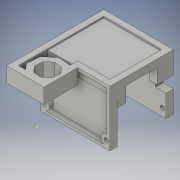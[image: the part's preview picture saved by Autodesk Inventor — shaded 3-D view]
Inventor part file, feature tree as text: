
AUTODESK INVENTOR PART (.ipt)
format: ipt  version: 2016 (Build 200138000, 138)  size: 295,424 bytes
history: native  units: in
note: dims shown in document units (in); Inventor stores cm internally (conversion verified against a paired STEP export)
features: sketch x10, extrude x9, shell x2
ambient origin geometry x8: Origin, YZ Plane, XZ Plane, XY Plane, X Axis, Y Axis, Z Axis, Center Point
bodies: Solid1 (feature_tree)
feature tree (21):
  extrude  "Extrusion1"  Depth=1.264in
  extrude  "Extrusion2"  Depth=0.25in
  extrude  "Extrusion3"  Depth=2.148in
  extrude  "Extrusion4"  Depth=0.25in
  extrude  "Extrusion5"  Depth=0.25in
  extrude  "Extrusion6"  Depth=1.648in
  extrude  "Extrusion7"  Depth=0.25in
  extrude  "Extrusion8"  Depth=0.25in
  sketch  "Sketch9"  dims[d21=2.355in d22=1.3885in d23=0.0in d24=0.5115in d25=0.0in d26=2.355in]
  extrude  "Extrusion9"  Depth=1.3885in TaperAngle=0.0deg
  shell  "Shell1"  Thickness=0.5115in
  shell  "Shell2"  Thickness=2.355in
  sketch  "Sketch1"  dims[d0=1.1438in d1=1.264in]
  sketch  "Sketch2"  dims[d5=0.65in d6=0.25in]
  sketch  "Sketch3"  dims[d8=2.3545in d9=2.148in]
  sketch  "Sketch4"  dims[d10=2.3545in d11=0.25in]
  sketch  "Sketch5"  dims[d12=0.5in d13=0.25in]
  sketch  "Sketch6"  dims[d14=1.8545in d15=1.648in]
  sketch  "Sketch7"  dims[d16=0.25in d17=0.25in]
  sketch  "Sketch8"  dims[d18=0.5115in d19=0.0in d20=0.25in]
  sketch  "Sketch10"  dims[d27=0.5115in d28=1.9in d29=0.0in d30=1.3885in d31=0.0in d37=0.25in d38=0.0in d39=0.35in d40=0.75in d41=0.75in d42=1.6875in d43=0.0in d44=0.2615in d45=0.0in d52=5.824in d53=0.0in d54=0.133in d55=0.2438in d56=1.131in d57=0.2in d58=0.1in]
